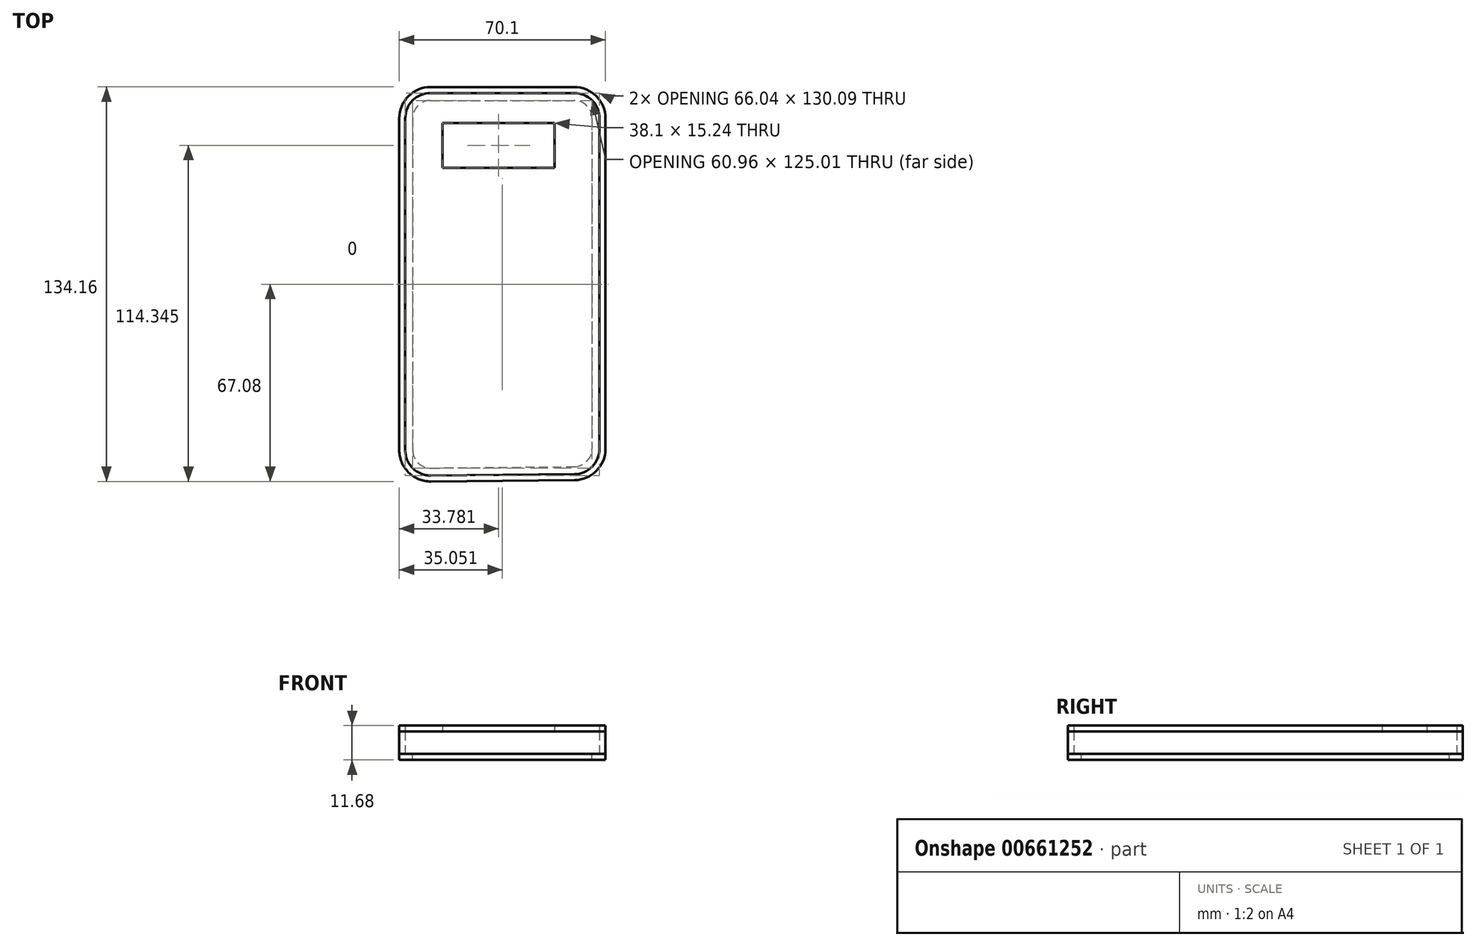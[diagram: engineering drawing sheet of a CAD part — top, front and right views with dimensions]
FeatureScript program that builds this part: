
annotation { "Feature Type Name" : "Feature", "Feature Type Description" : "" }
export const myFeature = defineFeature(function(context is Context, id is Id, definition is map)
    precondition{}
    {
        {
            var Q0;
            Q0=qCreatedBy(makeId("Top.planeOp"),FACE);
            var sketch = newSketch(context, id + "F0", { "sketchPlane" : qUnion([Q0])});
            skLineSegment(sketch, "E0", {"start": v(-33.75, 51.71) * mm, "end": v(15.02, 51.71) * mm});
            skLineSegment(sketch, "E1", {"start": v(23.65, 43.08) * mm, "end": v(23.65, -69.27) * mm});
            skLineSegment(sketch, "E2", {"start": v(-42.39, 43.08) * mm, "end": v(-42.39, -69.74) * mm});
            skLineSegment(sketch, "E3", {"start": v(-33.67, -78.38) * mm, "end": v(15.1, -77.9) * mm});
            skPoint(sketch, "E4.visualSharp", {"position": v(-42.39, 51.71) * mm});
            skArc(sketch, "E4.filletArc", {"start": v(-33.75, 51.71) * mm, "mid": v(-39.86, 49.19) * mm, "end": v(-42.39, 43.08) * mm});
            skPoint(sketch, "E5.visualSharp", {"position": v(23.65, 51.71) * mm});
            skArc(sketch, "E5.filletArc", {"start": v(23.65, 43.08) * mm, "mid": v(21.12, 49.19) * mm, "end": v(15.02, 51.71) * mm});
            skPoint(sketch, "E6.visualSharp", {"position": v(23.65, -77.83) * mm});
            skArc(sketch, "E6.filletArc", {"start": v(15.1, -77.9) * mm, "mid": v(21.15, -75.35) * mm, "end": v(23.65, -69.27) * mm});
            skPoint(sketch, "E7.visualSharp", {"position": v(-42.39, -78.46) * mm});
            skArc(sketch, "E7.filletArc", {"start": v(-42.39, -69.74) * mm, "mid": v(-39.83, -75.88) * mm, "end": v(-33.67, -78.38) * mm});
            skLineSegment(sketch, "E8.bottom", {"start": v(-29.69, 41.55) * mm, "end": v(8.41, 41.55) * mm});
            skLineSegment(sketch, "E8.top", {"start": v(-29.69, 26.31) * mm, "end": v(8.41, 26.31) * mm});
            skLineSegment(sketch, "E8.left", {"start": v(-29.69, 41.55) * mm, "end": v(-29.69, 26.31) * mm});
            skLineSegment(sketch, "E8.right", {"start": v(8.41, 41.55) * mm, "end": v(8.41, 26.31) * mm});
            skLineSegment(sketch, "E9.0", {"start": v(-33.75, 53.75) * mm, "end": v(15.02, 53.75) * mm});
            skArc(sketch, "E9.1", {"start": v(25.68, 43.08) * mm, "mid": v(22.56, 50.62) * mm, "end": v(15.02, 53.75) * mm});
            skArc(sketch, "E9.2", {"start": v(-33.75, 53.75) * mm, "mid": v(-41.3, 50.62) * mm, "end": v(-44.42, 43.08) * mm});
            skLineSegment(sketch, "E9.3", {"start": v(25.68, 43.08) * mm, "end": v(25.68, -69.27) * mm});
            skLineSegment(sketch, "E9.4", {"start": v(-44.42, 43.08) * mm, "end": v(-44.42, -69.74) * mm});
            skArc(sketch, "E9.5", {"start": v(-44.42, -69.74) * mm, "mid": v(-41.26, -77.32) * mm, "end": v(-33.65, -80.4) * mm});
            skLineSegment(sketch, "E9.6", {"start": v(-33.65, -80.4) * mm, "end": v(15.12, -79.94) * mm});
            skArc(sketch, "E9.7", {"start": v(15.12, -79.94) * mm, "mid": v(22.6, -76.78) * mm, "end": v(25.68, -69.27) * mm});
            skLineSegment(sketch, "E10.0", {"start": v(-33.75, 49.17) * mm, "end": v(15.02, 49.17) * mm});
            skArc(sketch, "E10.1", {"start": v(21.11, 43.08) * mm, "mid": v(19.33, 47.39) * mm, "end": v(15.02, 49.17) * mm});
            skArc(sketch, "E10.2", {"start": v(-33.75, 49.17) * mm, "mid": v(-38.06, 47.39) * mm, "end": v(-39.85, 43.08) * mm});
            skLineSegment(sketch, "E10.3", {"start": v(21.11, 43.08) * mm, "end": v(21.11, -69.27) * mm});
            skLineSegment(sketch, "E10.4", {"start": v(-39.85, 43.08) * mm, "end": v(-39.85, -69.74) * mm});
            skArc(sketch, "E10.5", {"start": v(-39.85, -69.74) * mm, "mid": v(-38.04, -74.07) * mm, "end": v(-33.7, -75.84) * mm});
            skLineSegment(sketch, "E10.6", {"start": v(-33.7, -75.84) * mm, "end": v(15.07, -75.37) * mm});
            skArc(sketch, "E10.7", {"start": v(15.07, -75.37) * mm, "mid": v(19.35, -73.56) * mm, "end": v(21.11, -69.27) * mm});
            skSolve(sketch);
        }
        {
            var Q0;
            Q0=makeQuery(id+"F0.imprint","IMPRINT",FACE,{"disambiguationData":[TD([[makeQuery(id+"F0.imprint","IMPRINT",EDGE,{"derivedFrom":sQuery(id+"F0.wireOp",EDGE,"E0")}),-1.0]])]});
            var Q1;
            Q1=makeQuery(id+"F0.imprint","IMPRINT",FACE,{"disambiguationData":[TD([[makeQuery(id+"F0.imprint","IMPRINT",EDGE,{"derivedFrom":sQuery(id+"F0.wireOp",EDGE,"E8.bottom")}),1.0]])]});
            extrude(context, id + "F1", {"entities" : qUnion([Q0, Q1]), "depth" : 7.62 * mm, "offsetDistance" : 25.4 * mm});
        }
        {
            var Q0;
            Q0=makeQuery(id+"F1.opExtrude","SWEPT_FACE",FACE,{"disambiguationData":[OSD([sQuery(id+"F0.wireOp",EDGE,"E1")])]});
            var sketch = newSketch(context, id + "F2", { "sketchPlane" : qUnion([Q0])});
            skLineSegment(sketch, "E11.bottom", {"start": v(26.31, 2.02) * mm, "end": v(6, 2.02) * mm});
            skLineSegment(sketch, "E11.top", {"start": v(26.31, 5.22) * mm, "end": v(6, 5.22) * mm});
            skLineSegment(sketch, "E11.left", {"start": v(26.31, 2.02) * mm, "end": v(26.31, 5.22) * mm});
            skLineSegment(sketch, "E11.right", {"start": v(6, 2.02) * mm, "end": v(6, 5.22) * mm});
            skPoint(sketch, "E12.0", {"position": v(51.71, 3.81) * mm});
            skLineSegment(sketch, "E13.0", {"start": v(51.71, 7.62) * mm, "end": v(51.71, 0) * mm});
            skSolve(sketch);
        }
        {
            var Q0;
            Q0=makeQuery(id+"F2.imprint","IMPRINT",FACE,{"disambiguationData":[TD([[makeQuery(id+"F2.imprint","IMPRINT",EDGE,{"derivedFrom":sQuery(id+"F2.wireOp",EDGE,"E11.bottom")}),-1.0]])]});
            extrude(context, id + "F3", {"entities" : qUnion([Q0]), "operationType" : NewBodyOperationType.ADD, "depth" : 25.4 * mm, "offsetDistance" : 25.4 * mm});
        }
        {
            var Q0;
            Q0=makeQuery(id+"F1.opExtrude","SWEPT_FACE",FACE,{"disambiguationData":[OSD([sQuery(id+"F0.wireOp",EDGE,"E3")])]});
            var sketch = newSketch(context, id + "F4", { "sketchPlane" : qUnion([Q0])});
            skLineSegment(sketch, "E14.0", {"start": v(-43.06, 7.62) * mm, "end": v(-43.06, 0) * mm});
            skLineSegment(sketch, "E15.0", {"start": v(-43.06, 0) * mm, "end": v(-34.42, 0) * mm});
            skLineSegment(sketch, "E16.0", {"start": v(-34.42, 0) * mm, "end": v(14.35, 0) * mm});
            skLineSegment(sketch, "E17.0", {"start": v(-43.06, 7.62) * mm, "end": v(-34.42, 7.62) * mm});
            skPoint(sketch, "E18.0", {"position": v(-29.44, 7.62) * mm});
            skLineSegment(sketch, "E19.0", {"start": v(-34.42, 7.62) * mm, "end": v(14.35, 7.62) * mm});
            skLineSegment(sketch, "E20.0", {"start": v(14.35, 7.62) * mm, "end": v(22.99, 7.62) * mm});
            skPoint(sketch, "E21.0", {"position": v(22.99, 0) * mm});
            skPoint(sketch, "E22.0", {"position": v(23.7, 2.02) * mm});
            skLineSegment(sketch, "E23.0", {"start": v(22.99, 7.62) * mm, "end": v(22.99, 0) * mm});
            skLineSegment(sketch, "E24.0", {"start": v(14.35, 0) * mm, "end": v(22.99, 0) * mm});
            skLineSegment(sketch, "E25.0.1", {"start": v(14.35, 0) * mm, "end": v(14.35, 7.62) * mm});
            skLineSegment(sketch, "E25.0.2", {"start": v(14.35, 7.62) * mm, "end": v(-34.42, 7.62) * mm});
            skLineSegment(sketch, "E25.0.3", {"start": v(-34.42, 7.62) * mm, "end": v(-34.42, 0) * mm});
            skLineSegment(sketch, "E26", {"start": v(-10.04, 7.62) * mm, "end": v(-10.04, 0) * mm});
            skLineSegment(sketch, "E27", {"start": v(-10.04, 6.35) * mm, "end": v(-13.85, 6.35) * mm});
            skLineSegment(sketch, "E28", {"start": v(-13.85, 6.35) * mm, "end": v(-13.85, 1.27) * mm});
            skLineSegment(sketch, "E29", {"start": v(-13.85, 1.27) * mm, "end": v(-6.23, 1.27) * mm});
            skLineSegment(sketch, "E30", {"start": v(-6.23, 1.27) * mm, "end": v(-6.23, 6.35) * mm});
            skLineSegment(sketch, "E31", {"start": v(-6.23, 6.35) * mm, "end": v(-10.04, 6.35) * mm});
            skCircle(sketch, "E32", {"center": v(3.93, 4.15) * mm, "radius": 1.88 * mm});
            skSolve(sketch);
        }
        {
            var Q0;
            Q0=makeQuery(id+"F1.opExtrude","SWEPT_FACE",FACE,{"disambiguationData":[OSD([sQuery(id+"F0.wireOp",EDGE,"E2")])]});
            var sketch = newSketch(context, id + "F5", { "sketchPlane" : qUnion([Q0])});
            skLineSegment(sketch, "E33.bottom", {"start": v(-13.61, 5.31) * mm, "end": v(-3.45, 5.31) * mm});
            skLineSegment(sketch, "E33.top", {"start": v(-13.61, 2.77) * mm, "end": v(-3.45, 2.77) * mm});
            skLineSegment(sketch, "E33.left", {"start": v(-13.61, 5.31) * mm, "end": v(-13.61, 2.77) * mm});
            skLineSegment(sketch, "E33.right", {"start": v(-3.45, 5.31) * mm, "end": v(-3.45, 2.77) * mm});
            skLineSegment(sketch, "E34.0.0", {"start": v(-51.71, 0) * mm, "end": v(-43.08, 0) * mm});
            skLineSegment(sketch, "E34.0.1", {"start": v(-43.08, 0) * mm, "end": v(-43.08, 7.62) * mm});
            skLineSegment(sketch, "E34.0.2", {"start": v(-43.08, 7.62) * mm, "end": v(-51.71, 7.62) * mm});
            skLineSegment(sketch, "E34.0.3", {"start": v(-51.71, 7.62) * mm, "end": v(-51.71, 0) * mm});
            skSolve(sketch);
        }
        {
            var Q0;
            Q0=makeQuery(id+"F5.imprint","IMPRINT",FACE,{"disambiguationData":[TD([[makeQuery(id+"F5.imprint","IMPRINT",EDGE,{"derivedFrom":sQuery(id+"F5.wireOp",EDGE,"E33.bottom")}),-1.0]])]});
            extrude(context, id + "F6", {"entities" : qUnion([Q0]), "operationType" : NewBodyOperationType.ADD, "depth" : 25.4 * mm, "offsetDistance" : 25.4 * mm});
        }
        {
            var Q0;
            {var subQ0=sQuery(id+"F4.wireOp",EDGE,"E27");Q0=makeQuery(id+"F4.imprint","IMPRINT",FACE,{"disambiguationData":[TD([[makeQuery(id+"F4.imprint","IMPRINT",EDGE,{"derivedFrom":subQ0}),1.0]])]});}
            var Q1;
            {var subQ4=sQuery(id+"F4.wireOp",EDGE,"E30");Q1=makeQuery(id+"F4.imprint","IMPRINT",FACE,{"disambiguationData":[TD([[makeQuery(id+"F4.imprint","IMPRINT",EDGE,{"derivedFrom":subQ4}),1.0]])]});}
            var Q2;
            Q2=makeQuery(id+"F4.imprint","IMPRINT",FACE,{"disambiguationData":[TD([[makeQuery(id+"F4.imprint","IMPRINT",EDGE,{"derivedFrom":sQuery(id+"F4.wireOp",EDGE,"E32")}),1.0]])]});
            extrude(context, id + "F7", {"entities" : qUnion([Q0, Q1, Q2]), "operationType" : NewBodyOperationType.ADD, "depth" : 25.4 * mm, "offsetDistance" : 25.4 * mm});
        }
        {
            var Q0;
            Q0=makeQuery(id+"F0.imprint","IMPRINT",FACE,{"disambiguationData":[TD([[makeQuery(id+"F0.imprint","IMPRINT",EDGE,{"derivedFrom":sQuery(id+"F0.wireOp",EDGE,"E0")}),1.0]])]});
            var Q1;
            Q1=makeQuery(id+"F1.opExtrude","CAP_FACE",FACE,{"disambiguationData":[OSD([sQuery(id+"F0.wireOp",EDGE,"E0"),sQuery(id+"F0.wireOp",EDGE,"E1"),sQuery(id+"F0.wireOp",EDGE,"E2"),sQuery(id+"F0.wireOp",EDGE,"E3"),sQuery(id+"F0.wireOp",EDGE,"E4.filletArc"),sQuery(id+"F0.wireOp",EDGE,"E5.filletArc"),sQuery(id+"F0.wireOp",EDGE,"E6.filletArc"),sQuery(id+"F0.wireOp",EDGE,"E7.filletArc"),sQuery(id+"F0.wireOp",EDGE,"E8.bottom"),sQuery(id+"F0.wireOp",EDGE,"E8.top"),sQuery(id+"F0.wireOp",EDGE,"E8.left"),sQuery(id+"F0.wireOp",EDGE,"E8.right")])],"isStart":false});
            extrude(context, id + "F8", {"entities" : qUnion([Q0]), "endBound" : BoundingType.UP_TO_SURFACE, "depth" : 25.4 * mm, "endBoundEntityFace" : qUnion([Q1]), "offsetDistance" : 25.4 * mm});
        }
        {
            var Q0;
            Q0=makeQuery(id+"F8.opExtrude","CAP_FACE",FACE,{"disambiguationData":[OSD([sQuery(id+"F0.wireOp",EDGE,"E0"),sQuery(id+"F0.wireOp",EDGE,"E1"),sQuery(id+"F0.wireOp",EDGE,"E2"),sQuery(id+"F0.wireOp",EDGE,"E3"),sQuery(id+"F0.wireOp",EDGE,"E4.filletArc"),sQuery(id+"F0.wireOp",EDGE,"E5.filletArc"),sQuery(id+"F0.wireOp",EDGE,"E6.filletArc"),sQuery(id+"F0.wireOp",EDGE,"E7.filletArc"),sQuery(id+"F0.wireOp",EDGE,"E9.0"),sQuery(id+"F0.wireOp",EDGE,"E9.1"),sQuery(id+"F0.wireOp",EDGE,"E9.2"),sQuery(id+"F0.wireOp",EDGE,"E9.3"),sQuery(id+"F0.wireOp",EDGE,"E9.4"),sQuery(id+"F0.wireOp",EDGE,"E9.5"),sQuery(id+"F0.wireOp",EDGE,"E9.6"),sQuery(id+"F0.wireOp",EDGE,"E9.7")])],"isStart":false});
            var Q1;
            Q1=makeQuery(id+"F1.opExtrude","CAP_FACE",FACE,{"disambiguationData":[OSD([sQuery(id+"F0.wireOp",EDGE,"E0"),sQuery(id+"F0.wireOp",EDGE,"E1"),sQuery(id+"F0.wireOp",EDGE,"E2"),sQuery(id+"F0.wireOp",EDGE,"E3"),sQuery(id+"F0.wireOp",EDGE,"E4.filletArc"),sQuery(id+"F0.wireOp",EDGE,"E5.filletArc"),sQuery(id+"F0.wireOp",EDGE,"E6.filletArc"),sQuery(id+"F0.wireOp",EDGE,"E7.filletArc"),sQuery(id+"F0.wireOp",EDGE,"E8.bottom"),sQuery(id+"F0.wireOp",EDGE,"E8.top"),sQuery(id+"F0.wireOp",EDGE,"E8.left"),sQuery(id+"F0.wireOp",EDGE,"E8.right")])],"isStart":false});
            extrude(context, id + "F9", {"entities" : qUnion([Q0, Q1]), "depth" : 2.03 * mm, "offsetDistance" : 25.4 * mm});
        }
        {
            var Q0;
            Q0=makeQuery(id+"F0.imprint","IMPRINT",FACE,{"disambiguationData":[TD([[makeQuery(id+"F0.imprint","IMPRINT",EDGE,{"derivedFrom":sQuery(id+"F0.wireOp",EDGE,"E0")}),-1.0]])]});
            var Q1;
            Q1=makeQuery(id+"F0.imprint","IMPRINT",FACE,{"disambiguationData":[TD([[makeQuery(id+"F0.imprint","IMPRINT",EDGE,{"derivedFrom":sQuery(id+"F0.wireOp",EDGE,"E0")}),1.0]])]});
            extrude(context, id + "F10", {"entities" : qUnion([Q0, Q1]), "oppositeDirection" : true, "depth" : 2.03 * mm, "offsetDistance" : 25.4 * mm});
        }
        {
            var Q0;
            Q0=makeQuery(id+"F1.opExtrude","SWEPT_BODY",BODY,{"disambiguationData":[OSD([sQuery(id+"F0.wireOp",EDGE,"E0"),sQuery(id+"F0.wireOp",EDGE,"E1"),sQuery(id+"F0.wireOp",EDGE,"E2"),sQuery(id+"F0.wireOp",EDGE,"E3"),sQuery(id+"F0.wireOp",EDGE,"E4.filletArc"),sQuery(id+"F0.wireOp",EDGE,"E5.filletArc"),sQuery(id+"F0.wireOp",EDGE,"E6.filletArc"),sQuery(id+"F0.wireOp",EDGE,"E7.filletArc"),sQuery(id+"F0.wireOp",EDGE,"E8.bottom"),sQuery(id+"F0.wireOp",EDGE,"E8.top"),sQuery(id+"F0.wireOp",EDGE,"E8.left"),sQuery(id+"F0.wireOp",EDGE,"E8.right")])]});
            var Q1;
            {var subQ0=sQuery(id+"F0.wireOp",EDGE,"E8.right");var subQ1=sQuery(id+"F0.wireOp",EDGE,"E8.left");var subQ2=sQuery(id+"F0.wireOp",EDGE,"E8.top");var subQ3=sQuery(id+"F0.wireOp",EDGE,"E8.bottom");var subQ4=sQuery(id+"F0.wireOp",EDGE,"E7.filletArc");var subQ5=sQuery(id+"F0.wireOp",EDGE,"E6.filletArc");var subQ6=sQuery(id+"F0.wireOp",EDGE,"E5.filletArc");var subQ7=sQuery(id+"F0.wireOp",EDGE,"E4.filletArc");var subQ8=sQuery(id+"F0.wireOp",EDGE,"E3");var subQ9=sQuery(id+"F0.wireOp",EDGE,"E2");var subQ10=sQuery(id+"F0.wireOp",EDGE,"E1");var subQ11=sQuery(id+"F0.wireOp",EDGE,"E0");Q1=makeQuery(id+"F9.opExtrude","SWEPT_BODY",BODY,{"disambiguationData":[OSD([subQ11,subQ10,subQ9,subQ8,subQ7,subQ6,subQ5,subQ4,subQ3,subQ2,subQ1,subQ0]),TDD([makeQuery(id+"F1.opExtrude","CAP_FACE",FACE,{"disambiguationData":[OSD([subQ11,subQ10,subQ9,subQ8,subQ7,subQ6,subQ5,subQ4,subQ3,subQ2,subQ1,subQ0])],"isStart":false})])]});}
            booleanBodies(context, id + "F11", {"operationType" : BooleanOperationType.SUBTRACTION, "tools" : qUnion([Q0]), "targets" : qUnion([Q1])});
        }
    });
